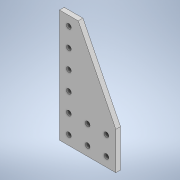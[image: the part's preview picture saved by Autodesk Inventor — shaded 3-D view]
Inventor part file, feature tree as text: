
AUTODESK INVENTOR PART (.ipt)
format: ipt  version: 2020 (Build 240168000, 168)  size: 124,416 bytes
history: native  units: in
note: dims shown in document units (in); Inventor stores cm internally (conversion verified against a paired STEP export)
features: extrude x1, sketch x1
ambient origin geometry x8: Origin, YZ Plane, XZ Plane, XY Plane, X Axis, Y Axis, Z Axis, Center Point
bodies: Solid1 (feature_tree)
feature tree (2):
  extrude  "Extrusion1"  Depth=0.25in
  sketch  "Sketch1"  dims[d4=4.0in d5=2.0in d6=1.0in d7=2.0in d8=4.0in d9=2.0in d10=3.0in d11=0.256in d12=0.5in d13=0.5in d14=2.3622in d16=1.0in d17=0.3937in d19=1.0in d21=1.1811in d23=1.0in d24=0.7874in d26=1.0in d29=0.25in d30=0.0in]
